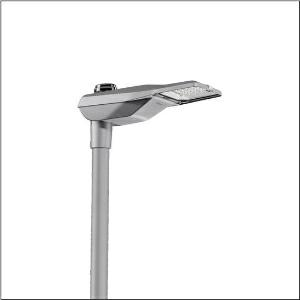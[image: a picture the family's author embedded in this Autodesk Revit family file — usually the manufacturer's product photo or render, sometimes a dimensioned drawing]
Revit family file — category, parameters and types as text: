
# Revit family: streetlight_sl_21_micro___st1_5a_5xe5p47n08cb_4c70
name_source: partatom
category: Lighting Fixtures
units: mm (PartAtom-declared; Revit-internal decimal feet)

## family parameters
Cut with Voids When Loaded = No
Host = Face
Light Source = No
Part Type = Normal
Room Calculation Point = No
Round Connector Dimension = Use Diameter
Shared = No

## types (1)
- --- (1 x LED, 2340 lm, 15.8 W, 4000K)
    Apparent Load = 16 VA
    CIE Flux Codes = 22 53 95 100 100
    Color Rendering = 70
    Color Temperature = 4000K
    Default Elevation = 1800 mm
    Description = Streetlight SL 21 micro, mast luminaire, primary light control with lens, of PMMA, primary optical cover: cover, of toughened safety glass, transparent, light distribution: ST1.5a, light emission: direct distribution, primary light characteristic: asymmetric, installation type: post-top, LED, 3G 1.5mm², High Power LED, rated luminous flux: 2.340lm, luminous efficacy: 148lm/W, light colour: 740, colour temperature: 4000K, control: overheat protection, pre-setting: linear dimming characteristic, constant luminous flux control, time-dependent luminous flux control, flexible luminous flux parameterisation, mains connection: 230..240V, AC, 50/60Hz, connection cable pre-assembled, cable length: 6,5m, wiring characteristics: H07RN-F, start of lifetime: 16W, end of service life: 16W, reduction: 8W, luminaire housing, of diecast aluminium (EN AC-44300), powder-coated, Siteco® metallic grey (DB 702S), corrosivity category C5 mid according to DIN EN ISO 12944, multi-level sealing system, sealing non-destructively replaceable, inclination adjustable: 0°, 5°, 10°, 15°, length: 528mm, width: 235mm, height: 110mm, spigot size: 76/60mm (post-top), protection rating (complete): IP66, insulation class (complete): insulation class I (protective earthing), certification: CE, ENEC, ENEC+, VDE, impact resistance: IK09, permissible operating ambient temperature for outdoor applications: -40..+50°C, standard-compliant lighting for roads and squares, packaging unit: 1 piece

Light Distribution: ST1.5a
    Height = 110 mm
    Lamp = 1 x LED
    Lamp Light Flux = 2340 lm
    Lamp Power = 15.8 W
    Lamp count = 1
    Length = 528 mm
    Luminous efficacy = 148 lm/W
    Manufacturer = Siteco
    ModVariant = No
    Model = 5XE5P47N08CB
    Number of Poles = 1
    OnlyDefault = Yes
    Power Factor = 1
    Product Name = Streetlight SL 21 micro | ST1.5a
    Product group = mast luminaire | pylon top
    ProductGroupID = 6100
    Protection Class = Protection class I
    Protection Degree = IP 66
    RLX_Detail_Level = 1
    RLX_Emergency_Light_Flux = 0 lm
    RLX_Emergency_Type = 0
    RLX_Emergency_Type_DB = No
    RlxData = <blob elided: 102625 chars, md5=bd46a3de>
    Socket = socket
    Standby Power = 0 W
    System Light Flux = 2340 lm
    System Power = 16 W
    Type Comments = factory setting: luminous flux: 100 % | dim-lin: 254 | 300 mA
    Type Image = l_1294375.jpg
    URL = http://relux.com
    VarID = @adj_103537
    Voltage = 0 V
    Weight = 0.00 kg
    Width = 235 mm

## geometry (parser evidence)
native form markers: Blend x4, Sweep x10
no freeform markers — native parametric forms only
